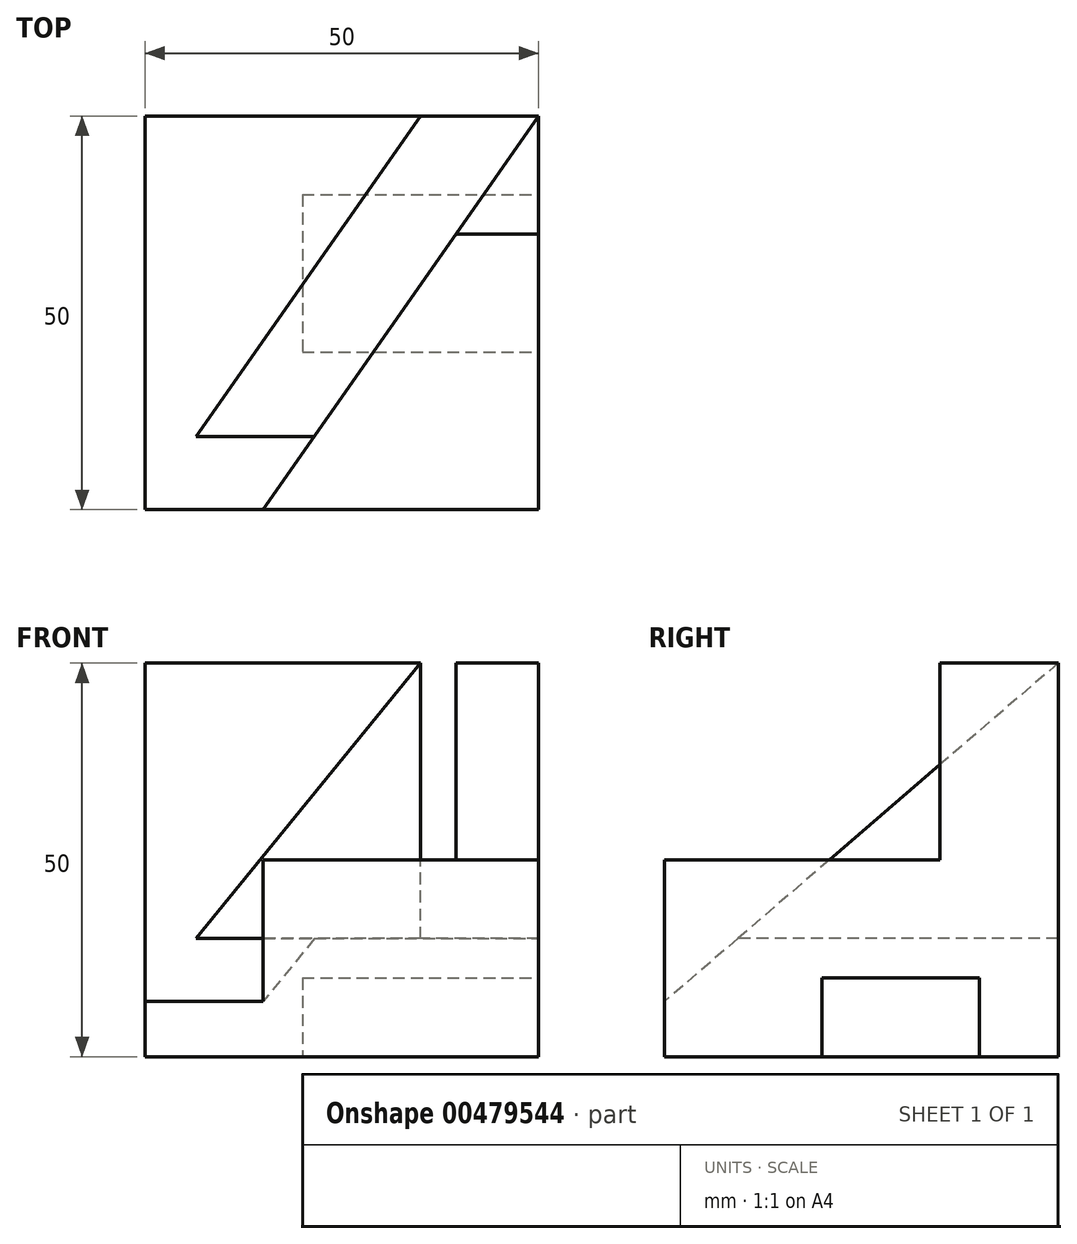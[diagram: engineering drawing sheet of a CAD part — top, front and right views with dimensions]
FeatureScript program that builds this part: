
annotation { "Feature Type Name" : "Feature", "Feature Type Description" : "" }
export const myFeature = defineFeature(function(context is Context, id is Id, definition is map)
    precondition{}
    {
        {
            var Q0;
            Q0=qCreatedBy(makeId("Right.planeOp"),FACE);
            cPlane(context, id + "F0", {"entities" : qUnion([Q0]), "cplaneType" : CPlaneType.OFFSET, "offset" : 20 * mm, "width" : 150 * mm, "height" : 150 * mm});
        }
        {
            var Q0;
            Q0=qCreatedBy(makeId("Top.planeOp"),FACE);
            cPlane(context, id + "F1", {"entities" : qUnion([Q0]), "cplaneType" : CPlaneType.OFFSET, "offset" : 15 * mm, "width" : 150 * mm, "height" : 150 * mm});
        }
        {
            var Q0;
            Q0=qCreatedBy(makeId("Top.planeOp"),FACE);
            cPlane(context, id + "F2", {"entities" : qUnion([Q0]), "cplaneType" : CPlaneType.OFFSET, "offset" : 25 * mm, "width" : 150 * mm, "height" : 150 * mm});
        }
        {
            var Q0;
            Q0=qCreatedBy(makeId("Top.planeOp"),FACE);
            var sketch = newSketch(context, id + "F3", { "sketchPlane" : qUnion([Q0])});
            skLineSegment(sketch, "E0.bottom", {"start": v(0, 0) * mm, "end": v(50, 0) * mm});
            skLineSegment(sketch, "E0.top", {"start": v(0, 50) * mm, "end": v(50, 50) * mm});
            skLineSegment(sketch, "E0.left", {"start": v(0, 0) * mm, "end": v(0, 50) * mm});
            skLineSegment(sketch, "E0.right", {"start": v(50, 0) * mm, "end": v(50, 50) * mm});
            skSolve(sketch);
        }
        {
            var Q0;
            Q0 = qSketchRegion(id + "F3", true);
            extrude(context, id + "F4", {"entities" : qUnion([Q0]), "depth" : 50 * mm});
        }
        {
            var Q0;
            Q0=makeQuery(id+"F4.opExtrude","SWEPT_FACE",FACE,{"disambiguationData":[OSD([sQuery(id+"F3.wireOp",EDGE,"E0.right")])]});
            var sketch = newSketch(context, id + "F5", { "sketchPlane" : qUnion([Q0])});
            skLineSegment(sketch, "E1.bottom", {"start": v(20, 0) * mm, "end": v(40, 0) * mm});
            skLineSegment(sketch, "E1.top", {"start": v(20, 10) * mm, "end": v(40, 10) * mm});
            skLineSegment(sketch, "E1.left", {"start": v(20, 0) * mm, "end": v(20, 10) * mm});
            skLineSegment(sketch, "E1.right", {"start": v(40, 0) * mm, "end": v(40, 10) * mm});
            skSolve(sketch);
        }
        {
            var Q0;
            Q0=makeQuery(id+"F5.imprint","IMPRINT",FACE,{"disambiguationData":[TD([[makeQuery(id+"F5.imprint","IMPRINT",EDGE,{"derivedFrom":sQuery(id+"F5.wireOp",EDGE,"E1.bottom")}),1.0]])]});
            var Q1;
            Q1 = qSketchRegion(id + "F5", true);
            var Q2;
            Q2=qCreatedBy(id+"F0.planeOp",FACE);
            extrude(context, id + "F6", {"entities" : qUnion([Q0, Q1]), "operationType" : NewBodyOperationType.REMOVE, "endBound" : BoundingType.UP_TO_SURFACE, "oppositeDirection" : true, "endBoundEntityFace" : qUnion([Q2]), "depth" : 25 * mm});
        }
        {
            var Q0;
            Q0=makeQuery(id+"F4.opExtrude","CAP_FACE",FACE,{"disambiguationData":[OSD([sQuery(id+"F3.wireOp",EDGE,"E0.bottom"),sQuery(id+"F3.wireOp",EDGE,"E0.top"),sQuery(id+"F3.wireOp",EDGE,"E0.left"),sQuery(id+"F3.wireOp",EDGE,"E0.right")])],"isStart":false});
            var sketch = newSketch(context, id + "F7", { "sketchPlane" : qUnion([Q0])});
            skLineSegment(sketch, "E2", {"start": v(50, 50) * mm, "end": v(15, 0) * mm});
            skLineSegment(sketch, "E3", {"start": v(15, 0) * mm, "end": v(0, 0) * mm});
            skLineSegment(sketch, "E4", {"start": v(0, 0) * mm, "end": v(35, 50) * mm});
            skLineSegment(sketch, "E5", {"start": v(35, 50) * mm, "end": v(50, 50) * mm});
            skSolve(sketch);
        }
        {
            var Q0;
            Q0=makeQuery(id+"F7.imprint","IMPRINT",FACE,{"disambiguationData":[TD([[makeQuery(id+"F7.imprint","IMPRINT",EDGE,{"derivedFrom":sQuery(id+"F7.wireOp",EDGE,"E2")}),-1.0]])]});
            var Q1;
            Q1=qCreatedBy(id+"F1.planeOp",FACE);
            extrude(context, id + "F8", {"entities" : qUnion([Q0]), "operationType" : NewBodyOperationType.REMOVE, "endBound" : BoundingType.UP_TO_SURFACE, "oppositeDirection" : true, "endBoundEntityFace" : qUnion([Q1]), "depth" : 25 * mm});
        }
        {
            var Q0;
            {var subQ0=sQuery(id+"F3.wireOp",EDGE,"E0.bottom");var subQ1=sQuery(id+"F3.wireOp",EDGE,"E0.right");Q0=makeQuery(id+"F8.boolean.opBoolean","SPLIT",FACE,{"disambiguationData":[TD([makeQuery(id+"F4.opExtrude","SWEPT_FACE",FACE,{"disambiguationData":[OSD([subQ0])]})])],"derivedFrom":makeQuery(id+"F4.opExtrude","CAP_FACE",FACE,{"disambiguationData":[OSD([subQ0,sQuery(id+"F3.wireOp",EDGE,"E0.top"),sQuery(id+"F3.wireOp",EDGE,"E0.left"),subQ1])],"isStart":false})});}
            var sketch = newSketch(context, id + "F9", { "sketchPlane" : qUnion([Q0])});
            skLineSegment(sketch, "E6", {"start": v(39.5, 35) * mm, "end": v(50, 35) * mm});
            skSolve(sketch);
        }
        {
            var Q0;
            {var subQ0=sQuery(id+"F9.wireOp",EDGE,"E6");Q0=makeQuery(id+"F9.imprint","IMPRINT",FACE,{"disambiguationData":[TD([[makeQuery(id+"F9.imprint","IMPRINT",EDGE,{"derivedFrom":subQ0}),-1.0]])]});}
            var Q1;
            Q1=qCreatedBy(id+"F2.planeOp",FACE);
            extrude(context, id + "F10", {"entities" : qUnion([Q0]), "operationType" : NewBodyOperationType.REMOVE, "endBound" : BoundingType.UP_TO_SURFACE, "oppositeDirection" : true, "endBoundEntityFace" : qUnion([Q1]), "depth" : 25 * mm});
        }
        {
            var Q0;
            Q0=makeQuery(id+"F4.opExtrude","SWEPT_FACE",FACE,{"disambiguationData":[OSD([sQuery(id+"F3.wireOp",EDGE,"E0.bottom")])]});
            var sketch = newSketch(context, id + "F11", { "sketchPlane" : qUnion([Q0])});
            skLineSegment(sketch, "E7.bottom", {"start": v(0, 0) * mm, "end": v(15, 0) * mm});
            skLineSegment(sketch, "E7.top", {"start": v(0, 7) * mm, "end": v(15, 7) * mm});
            skLineSegment(sketch, "E7.left", {"start": v(0, 0) * mm, "end": v(0, 7) * mm});
            skLineSegment(sketch, "E7.right", {"start": v(15, 0) * mm, "end": v(15, 7) * mm});
            skSolve(sketch);
        }
        {
            var Q0;
            Q0=sQuery(id+"F11.wireOp",EDGE,"E7.top");
            cPoint(context, id + "F12", {"entities" : qUnion([Q0]), "parameter" : 0.5});
        }
        {
            var Q0;
            Q0=makeQuery(id+"F4.opExtrude","CAP_VERTEX",VERTEX,{"disambiguationData":[OSD([sQuery(id+"F3.wireOp",EDGE,"E0.top"),sQuery(id+"F3.wireOp",EDGE,"E0.left")])],"isStart":false});
            var Q1;
            Q1=makeQuery(id+"F8.boolean.opBoolean","COPY",VERTEX,{"derivedFrom":makeQuery(id+"F8.opExtrude","CAP_VERTEX",VERTEX,{"disambiguationData":[OSD([sQuery(id+"F3.wireOp",EDGE,"E0.top"),sQuery(id+"F7.wireOp",EDGE,"E4"),sQuery(id+"F7.wireOp",EDGE,"E5")])],"isStart":true})});
            var Q2;
            Q2 = qCreatedBy(id + "F12" ,VERTEX);
            cPlane(context, id + "F13", {"entities" : qUnion([Q0, Q1, Q2]), "cplaneType" : CPlaneType.THREE_POINT, "offset" : 25 * mm, "width" : 150 * mm, "height" : 150 * mm});
        }
        {
            var Q0;
            {var subQ0=sQuery(id+"F3.wireOp",EDGE,"E0.top");var subQ1=sQuery(id+"F3.wireOp",EDGE,"E0.left");Q0=makeQuery(id+"F8.boolean.opBoolean","SPLIT",FACE,{"disambiguationData":[TD([makeQuery(id+"F4.opExtrude","SWEPT_FACE",FACE,{"disambiguationData":[OSD([subQ0])]})])],"derivedFrom":makeQuery(id+"F4.opExtrude","CAP_FACE",FACE,{"disambiguationData":[OSD([sQuery(id+"F3.wireOp",EDGE,"E0.bottom"),subQ0,subQ1,sQuery(id+"F3.wireOp",EDGE,"E0.right")])],"isStart":false})});}
            var Q1;
            Q1=qCreatedBy(id+"F13.planeOp",FACE);
            extrude(context, id + "F14", {"entities" : qUnion([Q0]), "operationType" : NewBodyOperationType.REMOVE, "endBound" : BoundingType.UP_TO_SURFACE, "oppositeDirection" : true, "endBoundEntityFace" : qUnion([Q1]), "depth" : 25 * mm});
        }
        {
            var Q0;
            Q0=makeQuery(id+"F8.boolean.opBoolean","COPY",FACE,{"derivedFrom":makeQuery(id+"F8.opExtrude","CAP_FACE",FACE,{"disambiguationData":[OSD([sQuery(id+"F7.wireOp",EDGE,"E2"),sQuery(id+"F7.wireOp",EDGE,"E3"),sQuery(id+"F7.wireOp",EDGE,"E4"),sQuery(id+"F7.wireOp",EDGE,"E5")])],"isStart":false})});
            var Q1;
            Q1=qCreatedBy(id+"F13.planeOp",FACE);
            extrude(context, id + "F15", {"entities" : qUnion([Q0]), "operationType" : NewBodyOperationType.REMOVE, "endBound" : BoundingType.UP_TO_SURFACE, "oppositeDirection" : true, "endBoundEntityFace" : qUnion([Q1]), "depth" : 25 * mm});
        }
    });
